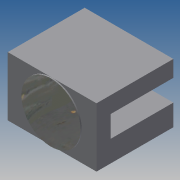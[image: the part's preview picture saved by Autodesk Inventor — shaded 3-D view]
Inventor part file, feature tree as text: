
AUTODESK INVENTOR PART (.ipt)
format: ipt  version: 2014 SP1 (Build 180222100, 222)  size: 103,424 bytes
history: native  units: in
note: dims shown in document units (in); Inventor stores cm internally (conversion verified against a paired STEP export)
features: sketch x3, extrude x2, hole x1
ambient origin geometry x8: Origin, YZ Plane, XZ Plane, XY Plane, X Axis, Y Axis, Z Axis, Center Point
bodies: Solid1 (feature_tree)
feature tree (6):
  extrude  "Extrusion1"  Depth=0.65in
  hole  "Hole1"  [1 undecoded]
  extrude  "Extrusion2"  Depth=0.01in TaperAngle=0.0deg
  sketch  "Sketch1"  dims[d0=0.5in d1=0.65in]
  sketch  "Sketch2"  dims[d2=0.75in d3=0.0in]
  sketch  "Sketch3"  dims[d4=0.13in d5=0.3in d6=0.375in d7=0.25in d8=0.5635in d9=0.3in d10=0.8108in d11=0.5in d12=0.01in d13=0.0in d14=0.12in]
note: 1 required parameter value undecoded (feature->parameter linkage not recoverable at this tier; creation-order binding heuristic only, values carry confidence <= 0.55)
